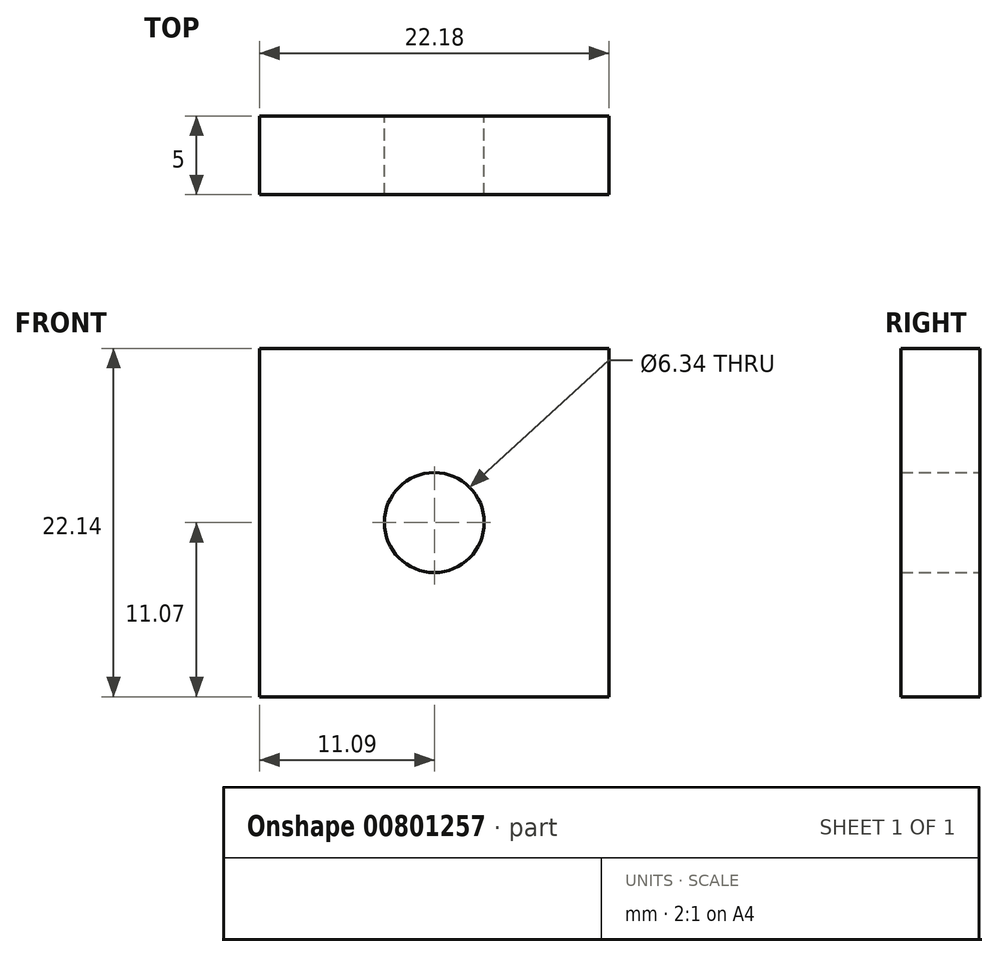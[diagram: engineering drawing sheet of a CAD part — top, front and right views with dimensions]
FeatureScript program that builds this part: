
annotation { "Feature Type Name" : "Feature", "Feature Type Description" : "" }
export const myFeature = defineFeature(function(context is Context, id is Id, definition is map)
    precondition{}
    {
        {
            var Q0;
            Q0=qCreatedBy(makeId("Front.planeOp"),FACE);
            var sketch = newSketch(context, id + "F0", { "sketchPlane" : qUnion([Q0])});
            skCircle(sketch, "E0", {"center": v(0, 0) * mm, "radius": 3.17 * mm});
            skSolve(sketch);
        }
        {
            var Q0;
            Q0=qCreatedBy(makeId("Front.planeOp"),FACE);
            var sketch = newSketch(context, id + "F1", { "sketchPlane" : qUnion([Q0])});
            skLineSegment(sketch, "E1.bottom", {"start": v(11.1, -11.07) * mm, "end": v(-11.1, -11.07) * mm});
            skLineSegment(sketch, "E1.top", {"start": v(11.1, 11.07) * mm, "end": v(-11.1, 11.07) * mm});
            skLineSegment(sketch, "E1.left", {"start": v(11.1, -11.07) * mm, "end": v(11.1, 11.07) * mm});
            skLineSegment(sketch, "E1.right", {"start": v(-11.1, -11.07) * mm, "end": v(-11.1, 11.07) * mm});
            skPoint(sketch, "E1.middle", {"position": v(0, 0) * mm});
            skSolve(sketch);
        }
        {
            var Q0;
            Q0 = qSketchRegion(id + "F1", true);
            extrude(context, id + "F2", {"entities" : qUnion([Q0]), "depth" : 5 * mm, "offsetDistance" : 25 * mm});
        }
        {
            var Q0;
            Q0 = qSketchRegion(id + "F0", true);
            extrude(context, id + "F3", {"entities" : qUnion([Q0]), "operationType" : NewBodyOperationType.REMOVE, "depth" : 25 * mm, "offsetDistance" : 25 * mm});
        }
    });
